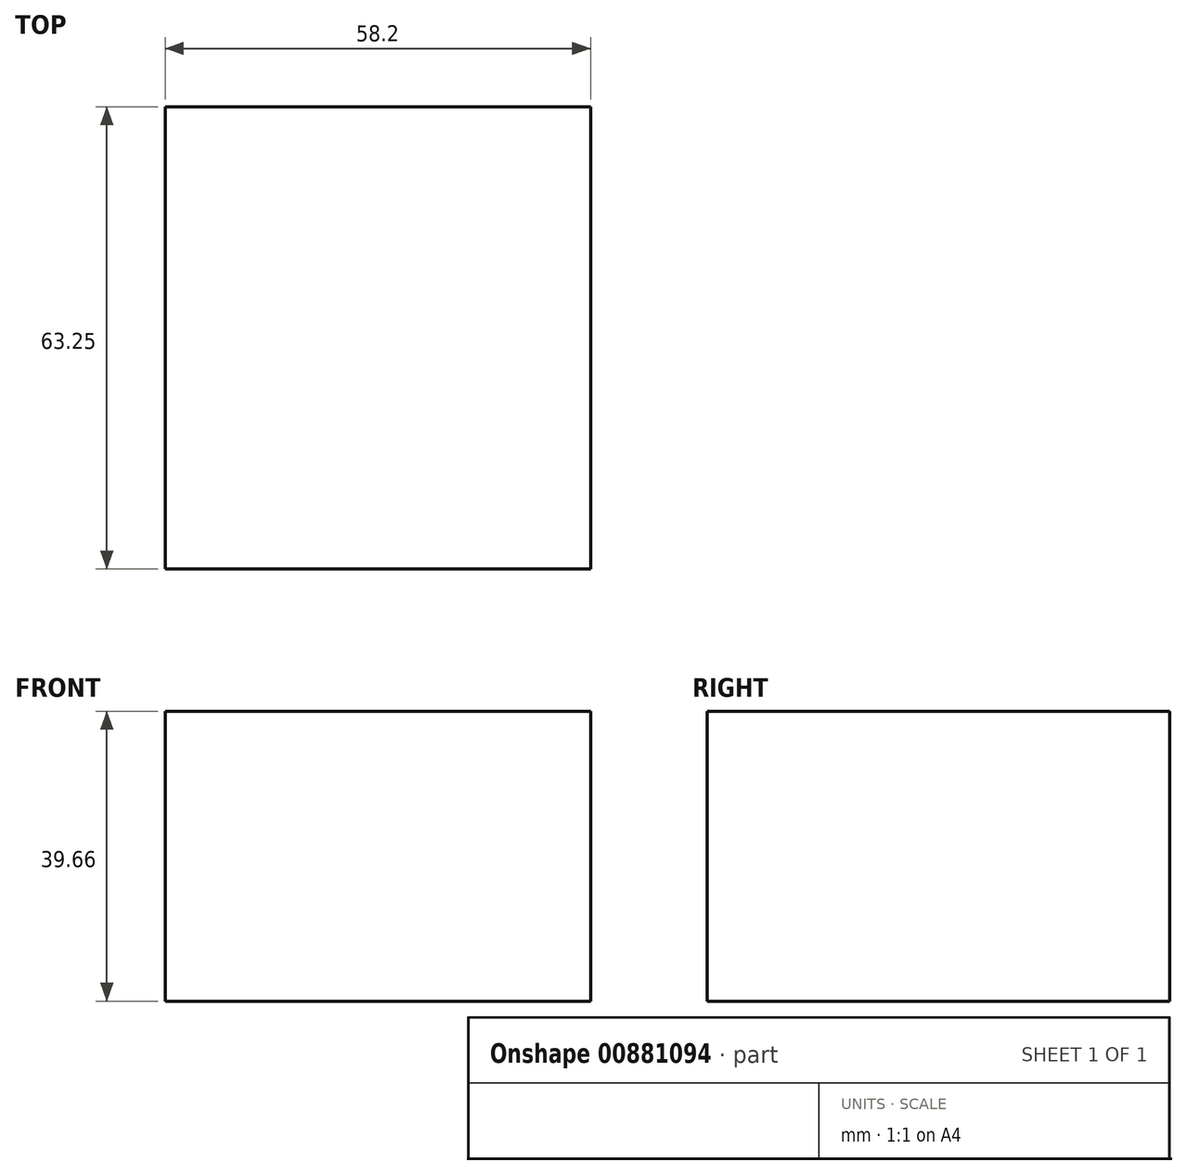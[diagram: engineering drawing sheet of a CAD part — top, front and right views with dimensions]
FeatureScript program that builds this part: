
annotation { "Feature Type Name" : "Feature", "Feature Type Description" : "" }
export const myFeature = defineFeature(function(context is Context, id is Id, definition is map)
    precondition{}
    {
        {
            var Q0;
            Q0=qCreatedBy(makeId("Top.planeOp"),FACE);
            var sketch = newSketch(context, id + "F0", { "sketchPlane" : qUnion([Q0])});
            skLineSegment(sketch, "E0.bottom", {"start": v(0, 0) * mm, "end": v(0, 0) * mm});
            skLineSegment(sketch, "E0.top", {"start": v(0, 0) * mm, "end": v(0, 0) * mm});
            skLineSegment(sketch, "E0.left", {"start": v(0, 0) * mm, "end": v(0, 0) * mm});
            skLineSegment(sketch, "E0.right", {"start": v(0, 0) * mm, "end": v(0, 0) * mm});
            skLineSegment(sketch, "E1.bottom", {"start": v(0, 0) * mm, "end": v(58.2, 0) * mm});
            skLineSegment(sketch, "E1.top", {"start": v(0, 63.25) * mm, "end": v(58.2, 63.25) * mm});
            skLineSegment(sketch, "E1.left", {"start": v(0, 0) * mm, "end": v(0, 63.25) * mm});
            skLineSegment(sketch, "E1.right", {"start": v(58.2, 0) * mm, "end": v(58.2, 63.25) * mm});
            skSolve(sketch);
        }
        {
            var Q0;
            Q0=makeQuery(id+"F0.imprint","IMPRINT",FACE,{"disambiguationData":[TD([[makeQuery(id+"F0.imprint","IMPRINT",EDGE,{"derivedFrom":sQuery(id+"F0.wireOp",EDGE,"E1.bottom")}),1.0]])]});
            extrude(context, id + "F1", {"entities" : qUnion([Q0]), "depth" : 39.66 * mm, "offsetDistance" : 25.4 * mm});
        }
    });
